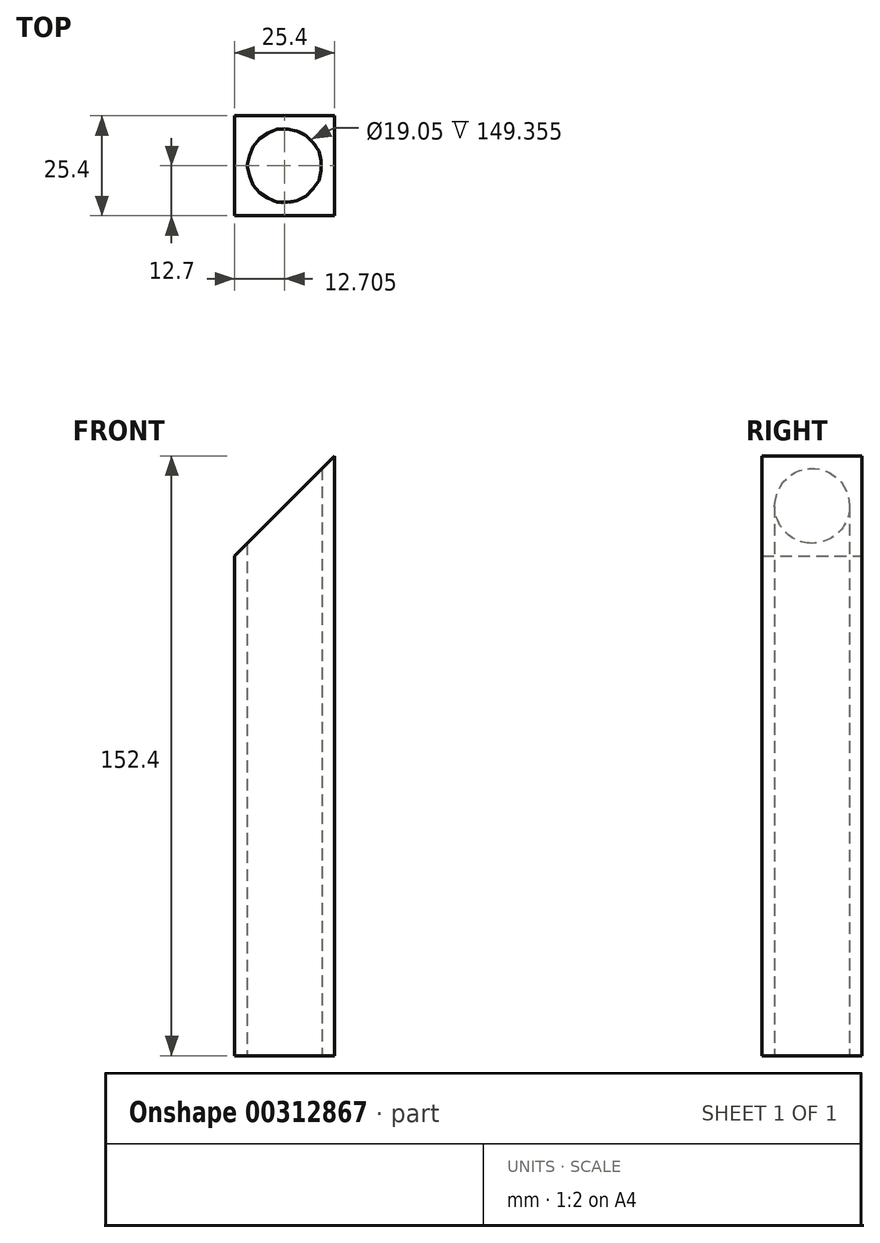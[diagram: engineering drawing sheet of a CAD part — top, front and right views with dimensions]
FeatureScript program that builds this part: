
annotation { "Feature Type Name" : "Feature", "Feature Type Description" : "" }
export const myFeature = defineFeature(function(context is Context, id is Id, definition is map)
    precondition{}
    {
        {
            var Q0;
            Q0=qCreatedBy(makeId("Front.planeOp"),FACE);
            var sketch = newSketch(context, id + "F0", { "sketchPlane" : qUnion([Q0])});
            skLineSegment(sketch, "E0", {"start": v(-16.48, -63.64) * mm, "end": v(-16.48, 63.36) * mm});
            skLineSegment(sketch, "E1", {"start": v(-16.48, 63.36) * mm, "end": v(8.92, 63.36) * mm});
            skLineSegment(sketch, "E2", {"start": v(8.92, 63.36) * mm, "end": v(8.92, -63.64) * mm});
            skLineSegment(sketch, "E3", {"start": v(8.92, -63.64) * mm, "end": v(-16.48, -63.64) * mm});
            skSolve(sketch);
        }
        {
            var Q0;
            Q0 = qSketchRegion(id + "F0", true);
            extrude(context, id + "F1", {"entities" : qUnion([Q0]), "endBound" : BoundingType.SYMMETRIC, "depth" : 25.4 * mm});
        }
        {
            var Q0;
            Q0=makeQuery(id+"F1.opExtrude","SWEPT_FACE",FACE,{"disambiguationData":[OSD([sQuery(id+"F0.wireOp",EDGE,"E3")])]});
            var sketch = newSketch(context, id + "F2", { "sketchPlane" : qUnion([Q0])});
            skCircle(sketch, "E4", {"center": v(-3.78, 0) * mm, "radius": 9.53 * mm});
            skPoint(sketch, "E4.centerSnap0", {"position": v(-3.78, 12.7) * mm});
            skSolve(sketch);
        }
        {
            var Q0;
            Q0=qCreatedBy(makeId("Front.planeOp"),FACE);
            var sketch = newSketch(context, id + "F3", { "sketchPlane" : qUnion([Q0])});
            skLineSegment(sketch, "E5.0.0", {"start": v(8.92, 63.36) * mm, "end": v(-16.48, 63.36) * mm});
            skLineSegment(sketch, "E5.0.2", {"start": v(-16.48, 63.36) * mm, "end": v(8.92, 63.36) * mm});
            skLineSegment(sketch, "E6", {"start": v(8.92, 63.36) * mm, "end": v(8.92, 88.76) * mm});
            skLineSegment(sketch, "E7", {"start": v(-16.48, 63.36) * mm, "end": v(8.92, 88.76) * mm});
            skSolve(sketch);
        }
        {
            var Q0;
            Q0 = qSketchRegion(id + "F3", true);
            extrude(context, id + "F4", {"entities" : qUnion([Q0]), "operationType" : NewBodyOperationType.ADD, "endBound" : BoundingType.SYMMETRIC, "depth" : 25.4 * mm});
        }
        {
            var Q0;
            Q0=makeQuery(id+"F2.imprint","IMPRINT",FACE,{"disambiguationData":[TD([[makeQuery(id+"F2.imprint","IMPRINT",EDGE,{"derivedFrom":sQuery(id+"F2.wireOp",EDGE,"E4")}),1.0]])]});
            extrude(context, id + "F5", {"entities" : qUnion([Q0]), "operationType" : NewBodyOperationType.REMOVE, "endBound" : BoundingType.THROUGH_ALL, "oppositeDirection" : true, "depth" : 114.3 * mm});
        }
    });
